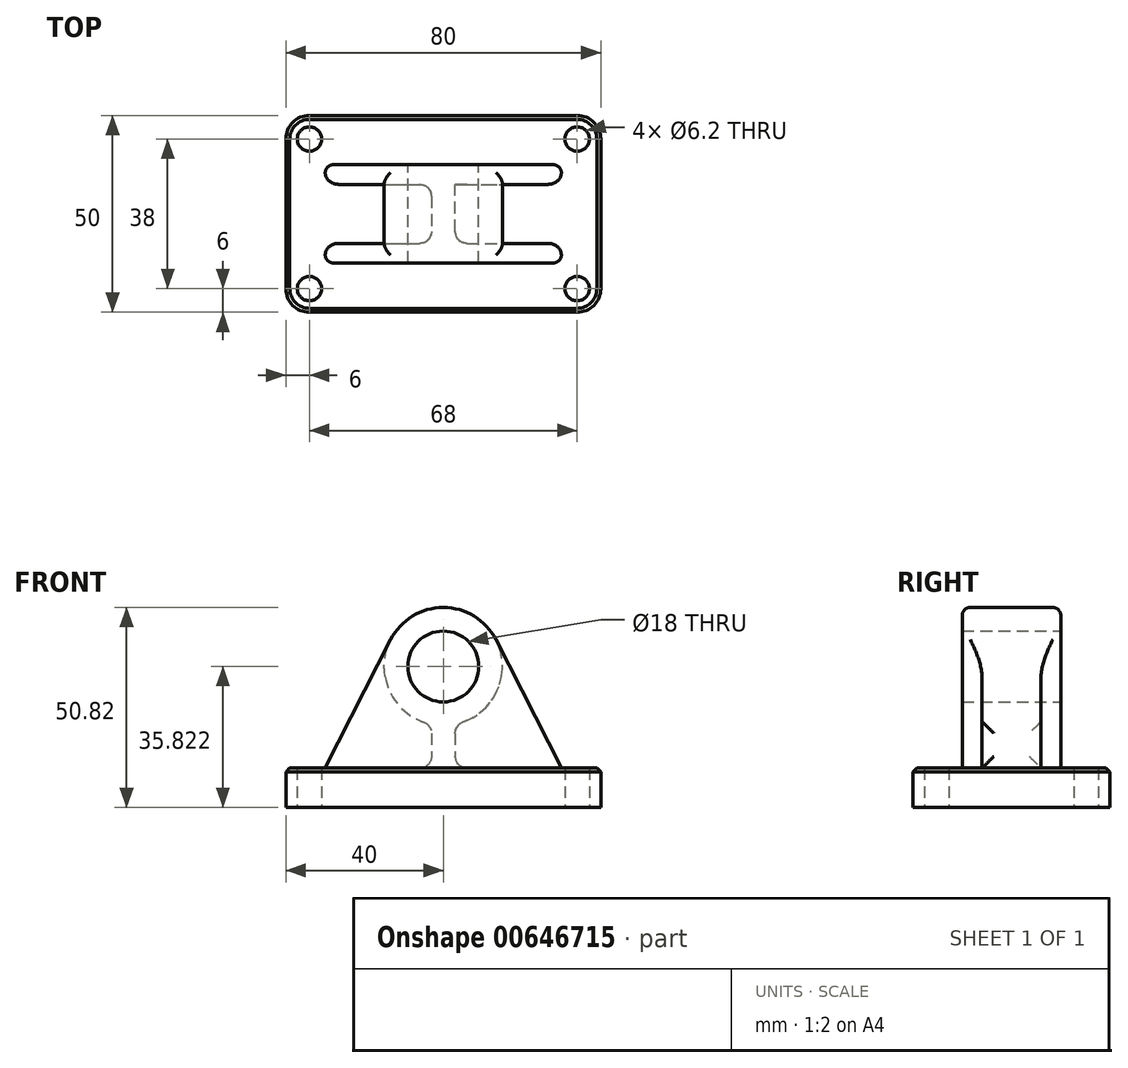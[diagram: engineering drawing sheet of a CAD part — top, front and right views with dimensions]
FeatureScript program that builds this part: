
annotation { "Feature Type Name" : "Feature", "Feature Type Description" : "" }
export const myFeature = defineFeature(function(context is Context, id is Id, definition is map)
    precondition{}
    {
        {
            var Q0;
            Q0=qCreatedBy(makeId("Top.planeOp"),FACE);
            var sketch = newSketch(context, id + "F0", { "sketchPlane" : qUnion([Q0])});
            skLineSegment(sketch, "E0.bottom", {"start": v(34, 25) * mm, "end": v(-34, 25) * mm});
            skLineSegment(sketch, "E0.top", {"start": v(34, -25) * mm, "end": v(-34, -25) * mm});
            skLineSegment(sketch, "E0.left", {"start": v(40, 19) * mm, "end": v(40, -19) * mm});
            skLineSegment(sketch, "E0.right", {"start": v(-40, 19) * mm, "end": v(-40, -19) * mm});
            skPoint(sketch, "E0.middle", {"position": v(0, 0) * mm});
            skPoint(sketch, "E1.visualSharp", {"position": v(-40, 25) * mm});
            skArc(sketch, "E1.filletArc", {"start": v(-34, 25) * mm, "mid": v(-38.24, 23.24) * mm, "end": v(-40, 19) * mm});
            skPoint(sketch, "E2.visualSharp", {"position": v(40, 25) * mm});
            skArc(sketch, "E2.filletArc", {"start": v(40, 19) * mm, "mid": v(38.24, 23.24) * mm, "end": v(34, 25) * mm});
            skPoint(sketch, "E3.visualSharp", {"position": v(40, -25) * mm});
            skArc(sketch, "E3.filletArc", {"start": v(34, -25) * mm, "mid": v(38.24, -23.24) * mm, "end": v(40, -19) * mm});
            skPoint(sketch, "E4.visualSharp", {"position": v(-40, -25) * mm});
            skArc(sketch, "E4.filletArc", {"start": v(-40, -19) * mm, "mid": v(-38.24, -23.24) * mm, "end": v(-34, -25) * mm});
            skCircle(sketch, "E5", {"center": v(-34, 19) * mm, "radius": 3.1 * mm});
            skCircle(sketch, "E6.0.1.0", {"center": v(-34, -19) * mm, "radius": 3.1 * mm});
            skCircle(sketch, "E6.1.0.0", {"center": v(34, 19) * mm, "radius": 3.1 * mm});
            skCircle(sketch, "E6.1.1.0", {"center": v(34, -19) * mm, "radius": 3.1 * mm});
            skLineSegment(sketch, "E6.direction1", {"start": v(-34, 19) * mm, "end": v(34, 19) * mm, "construction": true});
            skLineSegment(sketch, "E6.direction2", {"start": v(-34, 19) * mm, "end": v(-34, -19) * mm, "construction": true});
            skSolve(sketch);
        }
        {
            var Q0;
            Q0=makeQuery(id+"F0.imprint","IMPRINT",FACE,{"disambiguationData":[TD([[makeQuery(id+"F0.imprint","IMPRINT",EDGE,{"derivedFrom":sQuery(id+"F0.wireOp",EDGE,"E0.bottom")}),1.0]])]});
            extrude(context, id + "F1", {"entities" : qUnion([Q0]), "depth" : 10 * mm, "offsetDistance" : 25 * mm});
        }
        {
            var Q0;
            Q0=qCreatedBy(makeId("Front.planeOp"),FACE);
            var sketch = newSketch(context, id + "F2", { "sketchPlane" : qUnion([Q0])});
            skArc(sketch, "E7", {"start": v(3, 21.13) * mm, "mid": v(0, 50.82) * mm, "end": v(-3, 21.13) * mm});
            skCircle(sketch, "E8", {"center": v(0, 35.82) * mm, "radius": 9 * mm});
            skLineSegment(sketch, "E9.top", {"start": v(3, 4.74) * mm, "end": v(-3, 4.74) * mm});
            skLineSegment(sketch, "E9.left", {"start": v(3, 21.13) * mm, "end": v(3, 4.74) * mm});
            skLineSegment(sketch, "E9.right", {"start": v(-3, 21.13) * mm, "end": v(-3, 4.74) * mm});
            skPoint(sketch, "E9.middle", {"position": v(0, 14.08) * mm});
            skPoint(sketch, "E10.orphan", {"position": v(-3, 23.42) * mm});
            skPoint(sketch, "E11.orphan", {"position": v(3, 23.42) * mm});
            skSolve(sketch);
        }
        {
            var Q0;
            Q0 = qSketchRegion(id + "F2", true);
            extrude(context, id + "F3", {"entities" : qUnion([Q0]), "operationType" : NewBodyOperationType.ADD, "endBound" : BoundingType.SYMMETRIC, "depth" : 25 * mm, "offsetDistance" : 25 * mm});
        }
        {
            var Q0;
            Q0=makeQuery(id+"F3.opExtrude","CAP_FACE",FACE,{"disambiguationData":[OSD([sQuery(id+"F2.wireOp",EDGE,"E7"),sQuery(id+"F2.wireOp",EDGE,"E8"),sQuery(id+"F2.wireOp",EDGE,"E9.top"),sQuery(id+"F2.wireOp",EDGE,"E9.left"),sQuery(id+"F2.wireOp",EDGE,"E9.right")])],"isStart":false});
            var sketch = newSketch(context, id + "F4", { "sketchPlane" : qUnion([Q0])});
            skLineSegment(sketch, "E12", {"start": v(-30, 10) * mm, "end": v(-13.36, 42.63) * mm});
            skLineSegment(sketch, "E13", {"start": v(13.36, 42.63) * mm, "end": v(30, 10) * mm});
            skLineSegment(sketch, "E14", {"start": v(0, 0) * mm, "end": v(0, 53.81) * mm, "construction": true});
            skArc(sketch, "E15", {"start": v(-13.36, 42.63) * mm, "mid": v(0, 20.82) * mm, "end": v(13.36, 42.63) * mm});
            skLineSegment(sketch, "E16", {"start": v(-30, 10) * mm, "end": v(30, 10) * mm});
            skSolve(sketch);
        }
        {
            var Q0;
            Q0 = qSketchRegion(id + "F4", true);
            extrude(context, id + "F5", {"entities" : qUnion([Q0]), "operationType" : NewBodyOperationType.ADD, "oppositeDirection" : true, "depth" : 5 * mm, "offsetDistance" : 25 * mm});
        }
        {
            var Q0;
            Q0=makeQuery(id+"F1.opExtrude","SWEPT_BODY",BODY,{"disambiguationData":[OSD([sQuery(id+"F0.wireOp",EDGE,"E0.bottom"),sQuery(id+"F0.wireOp",EDGE,"E0.top"),sQuery(id+"F0.wireOp",EDGE,"E0.left"),sQuery(id+"F0.wireOp",EDGE,"E0.right"),sQuery(id+"F0.wireOp",EDGE,"E1.filletArc"),sQuery(id+"F0.wireOp",EDGE,"E2.filletArc"),sQuery(id+"F0.wireOp",EDGE,"E3.filletArc"),sQuery(id+"F0.wireOp",EDGE,"E4.filletArc"),sQuery(id+"F0.wireOp",EDGE,"E5"),sQuery(id+"F0.wireOp",EDGE,"E6.0.1.0"),sQuery(id+"F0.wireOp",EDGE,"E6.1.0.0"),sQuery(id+"F0.wireOp",EDGE,"E6.1.1.0")])]});
            var Q1;
            Q1=qCreatedBy(makeId("Front.planeOp"),FACE);
            mirror(context, id + "F6", {"operationType" : NewBodyOperationType.ADD, "entities" : qUnion([Q0]), "mirrorPlane" : qUnion([Q1])});
        }
        {
            var Q0;
            Q0=makeQuery(id+"F6.opPattern","COPY",EDGE,{"derivedFrom":makeQuery(id+"F5.opExtrude","CAP_EDGE",EDGE,{"disambiguationData":[OSD([sQuery(id+"F4.wireOp",EDGE,"E12")])],"isStart":true}),"instanceName":"1"});
            var Q1;
            Q1=makeQuery(id+"F3.opExtrude","CAP_EDGE",EDGE,{"disambiguationData":[OSD([sQuery(id+"F2.wireOp",EDGE,"E7")])],"isStart":false});
            fillet(context, id + "F7", {"entities" : qUnion([Q0, Q1]), "radius" : 2 * mm, "tangentPropagation" : true, "allowEdgeOverflow" : false});
        }
        {
            var Q0;
            Q0=makeQuery(id+"F3.opExtrude","SWEPT_FACE",FACE,{"disambiguationData":[OSD([sQuery(id+"F2.wireOp",EDGE,"E9.right")])]});
            var Q1;
            {var subQ1=sQuery(id+"F4.wireOp",EDGE,"E16");Q1=makeQuery(id+"F5.boolean.opBoolean","SPLIT",EDGE,{"disambiguationData":[TD([makeQuery(id+"F3.opExtrude","SWEPT_FACE",FACE,{"disambiguationData":[OSD([sQuery(id+"F2.wireOp",EDGE,"E9.right")])]})])],"derivedFrom":makeQuery(id+"F5.opExtrude","CAP_EDGE",EDGE,{"disambiguationData":[OSD([subQ1])],"isStart":false})});}
            var Q2;
            Q2=makeQuery(id+"F6.opPattern","COPY",EDGE,{"derivedFrom":makeQuery(id+"F5.opExtrude","SWEPT_EDGE",EDGE,{"disambiguationData":[OSD([sQuery(id+"F4.wireOp",EDGE,"E12"),sQuery(id+"F4.wireOp",EDGE,"E16")])]}),"instanceName":"1"});
            var Q3;
            Q3=makeQuery(id+"F5.opExtrude","SWEPT_EDGE",EDGE,{"disambiguationData":[OSD([sQuery(id+"F4.wireOp",EDGE,"E12"),sQuery(id+"F4.wireOp",EDGE,"E16")])]});
            var Q4;
            {var subQ1=sQuery(id+"F4.wireOp",EDGE,"E16");Q4=makeQuery(id+"F6.opPattern","COPY",EDGE,{"derivedFrom":makeQuery(id+"F5.boolean.opBoolean","SPLIT",EDGE,{"disambiguationData":[TD([makeQuery(id+"F3.opExtrude","SWEPT_FACE",FACE,{"disambiguationData":[OSD([sQuery(id+"F2.wireOp",EDGE,"E9.right")])]})])],"derivedFrom":makeQuery(id+"F5.opExtrude","CAP_EDGE",EDGE,{"disambiguationData":[OSD([subQ1])],"isStart":false})}),"instanceName":"1"});}
            var Q5;
            {var subQ0=sQuery(id+"F2.wireOp",EDGE,"E9.right");var subQ1=sQuery(id+"F2.wireOp",EDGE,"E9.left");var subQ2=sQuery(id+"F2.wireOp",EDGE,"E9.top");var subQ3=sQuery(id+"F2.wireOp",EDGE,"E8");var subQ4=sQuery(id+"F2.wireOp",EDGE,"E7");var subQ5=makeQuery(id+"F1.opExtrude","CAP_FACE",FACE,{"disambiguationData":[OSD([sQuery(id+"F0.wireOp",EDGE,"E0.bottom"),sQuery(id+"F0.wireOp",EDGE,"E0.top"),sQuery(id+"F0.wireOp",EDGE,"E0.left"),sQuery(id+"F0.wireOp",EDGE,"E0.right"),sQuery(id+"F0.wireOp",EDGE,"E1.filletArc"),sQuery(id+"F0.wireOp",EDGE,"E2.filletArc"),sQuery(id+"F0.wireOp",EDGE,"E3.filletArc"),sQuery(id+"F0.wireOp",EDGE,"E4.filletArc"),sQuery(id+"F0.wireOp",EDGE,"E5"),sQuery(id+"F0.wireOp",EDGE,"E6.0.1.0"),sQuery(id+"F0.wireOp",EDGE,"E6.1.0.0"),sQuery(id+"F0.wireOp",EDGE,"E6.1.1.0")])],"isStart":false});Q5=makeQuery(id+"F6.boolean.opBoolean","MERGE",EDGE,{"derivedFrom":[makeQuery(id+"F3.boolean.opBoolean","INTERSECT",EDGE,{"derivedFrom":[subQ5,makeQuery(id+"F3.opExtrude","CAP_FACE",FACE,{"disambiguationData":[OSD([subQ4,subQ3,subQ2,subQ1,subQ0])],"isStart":true})]}),makeQuery(id+"F6.opPattern","COPY",EDGE,{"derivedFrom":makeQuery(id+"F5.boolean.opBoolean","MERGE",EDGE,{"derivedFrom":[makeQuery(id+"F3.boolean.opBoolean","INTERSECT",EDGE,{"derivedFrom":[subQ5,makeQuery(id+"F3.opExtrude","CAP_FACE",FACE,{"disambiguationData":[OSD([subQ4,subQ3,subQ2,subQ1,subQ0])],"isStart":false})]}),makeQuery(id+"F5.opExtrude","CAP_EDGE",EDGE,{"disambiguationData":[OSD([sQuery(id+"F4.wireOp",EDGE,"E16")])],"isStart":true})]}),"instanceName":"1"})]});}
            var Q6;
            Q6=makeQuery(id+"F6.opPattern","COPY",EDGE,{"derivedFrom":makeQuery(id+"F5.opExtrude","SWEPT_EDGE",EDGE,{"disambiguationData":[OSD([sQuery(id+"F4.wireOp",EDGE,"E13"),sQuery(id+"F4.wireOp",EDGE,"E16")])]}),"instanceName":"1"});
            var Q7;
            {var subQ0=sQuery(id+"F4.wireOp",EDGE,"E16");Q7=makeQuery(id+"F6.opPattern","COPY",EDGE,{"derivedFrom":makeQuery(id+"F5.boolean.opBoolean","SPLIT",EDGE,{"disambiguationData":[TD([makeQuery(id+"F3.opExtrude","SWEPT_FACE",FACE,{"disambiguationData":[OSD([sQuery(id+"F2.wireOp",EDGE,"E9.left")])]})])],"derivedFrom":makeQuery(id+"F5.opExtrude","CAP_EDGE",EDGE,{"disambiguationData":[OSD([subQ0])],"isStart":false})}),"instanceName":"1"});}
            var Q8;
            {var subQ0=sQuery(id+"F4.wireOp",EDGE,"E15");Q8=makeQuery(id+"F6.opPattern","COPY",EDGE,{"derivedFrom":makeQuery(id+"F5.boolean.opBoolean","SPLIT",EDGE,{"disambiguationData":[TD([makeQuery(id+"F3.opExtrude","SWEPT_FACE",FACE,{"disambiguationData":[OSD([sQuery(id+"F2.wireOp",EDGE,"E9.left")])]})])],"derivedFrom":makeQuery(id+"F5.opExtrude","CAP_EDGE",EDGE,{"disambiguationData":[OSD([subQ0])],"isStart":false})}),"instanceName":"1"});}
            var Q9;
            Q9=makeQuery(id+"F3.boolean.opBoolean","INTERSECT",EDGE,{"derivedFrom":[makeQuery(id+"F1.opExtrude","CAP_FACE",FACE,{"disambiguationData":[OSD([sQuery(id+"F0.wireOp",EDGE,"E0.bottom"),sQuery(id+"F0.wireOp",EDGE,"E0.top"),sQuery(id+"F0.wireOp",EDGE,"E0.left"),sQuery(id+"F0.wireOp",EDGE,"E0.right"),sQuery(id+"F0.wireOp",EDGE,"E1.filletArc"),sQuery(id+"F0.wireOp",EDGE,"E2.filletArc"),sQuery(id+"F0.wireOp",EDGE,"E3.filletArc"),sQuery(id+"F0.wireOp",EDGE,"E4.filletArc"),sQuery(id+"F0.wireOp",EDGE,"E5"),sQuery(id+"F0.wireOp",EDGE,"E6.0.1.0"),sQuery(id+"F0.wireOp",EDGE,"E6.1.0.0"),sQuery(id+"F0.wireOp",EDGE,"E6.1.1.0")])],"isStart":false}),makeQuery(id+"F3.opExtrude","SWEPT_FACE",FACE,{"disambiguationData":[OSD([sQuery(id+"F2.wireOp",EDGE,"E9.left")])]})]});
            var Q10;
            Q10=makeQuery(id+"F5.boolean.opBoolean","INTERSECT",EDGE,{"derivedFrom":[makeQuery(id+"F3.opExtrude","SWEPT_FACE",FACE,{"disambiguationData":[OSD([sQuery(id+"F2.wireOp",EDGE,"E9.left")])]}),makeQuery(id+"F5.opExtrude","CAP_FACE",FACE,{"disambiguationData":[OSD([sQuery(id+"F4.wireOp",EDGE,"E12"),sQuery(id+"F4.wireOp",EDGE,"E13"),sQuery(id+"F4.wireOp",EDGE,"E15"),sQuery(id+"F4.wireOp",EDGE,"E16")])],"isStart":false})]});
            var Q11;
            {var subQ0=sQuery(id+"F4.wireOp",EDGE,"E16");Q11=makeQuery(id+"F5.boolean.opBoolean","SPLIT",EDGE,{"disambiguationData":[TD([makeQuery(id+"F3.opExtrude","SWEPT_FACE",FACE,{"disambiguationData":[OSD([sQuery(id+"F2.wireOp",EDGE,"E9.left")])]})])],"derivedFrom":makeQuery(id+"F5.opExtrude","CAP_EDGE",EDGE,{"disambiguationData":[OSD([subQ0])],"isStart":false})});}
            var Q12;
            Q12=makeQuery(id+"F3.opExtrude","SWEPT_EDGE",EDGE,{"disambiguationData":[OSD([sQuery(id+"F2.wireOp",EDGE,"E7"),sQuery(id+"F2.wireOp",EDGE,"E9.left")])]});
            var Q13;
            {var subQ0=sQuery(id+"F4.wireOp",EDGE,"E15");Q13=makeQuery(id+"F5.boolean.opBoolean","SPLIT",EDGE,{"disambiguationData":[TD([makeQuery(id+"F3.opExtrude","SWEPT_FACE",FACE,{"disambiguationData":[OSD([sQuery(id+"F2.wireOp",EDGE,"E9.left")])]})])],"derivedFrom":makeQuery(id+"F5.opExtrude","CAP_EDGE",EDGE,{"disambiguationData":[OSD([subQ0])],"isStart":false})});}
            var Q14;
            Q14=makeQuery(id+"F5.opExtrude","SWEPT_EDGE",EDGE,{"disambiguationData":[OSD([sQuery(id+"F4.wireOp",EDGE,"E13"),sQuery(id+"F4.wireOp",EDGE,"E16")])]});
            var Q15;
            Q15=makeQuery(id+"F5.boolean.opBoolean","MERGE",EDGE,{"derivedFrom":[makeQuery(id+"F3.boolean.opBoolean","INTERSECT",EDGE,{"derivedFrom":[makeQuery(id+"F1.opExtrude","CAP_FACE",FACE,{"disambiguationData":[OSD([sQuery(id+"F0.wireOp",EDGE,"E0.bottom"),sQuery(id+"F0.wireOp",EDGE,"E0.top"),sQuery(id+"F0.wireOp",EDGE,"E0.left"),sQuery(id+"F0.wireOp",EDGE,"E0.right"),sQuery(id+"F0.wireOp",EDGE,"E1.filletArc"),sQuery(id+"F0.wireOp",EDGE,"E2.filletArc"),sQuery(id+"F0.wireOp",EDGE,"E3.filletArc"),sQuery(id+"F0.wireOp",EDGE,"E4.filletArc"),sQuery(id+"F0.wireOp",EDGE,"E5"),sQuery(id+"F0.wireOp",EDGE,"E6.0.1.0"),sQuery(id+"F0.wireOp",EDGE,"E6.1.0.0"),sQuery(id+"F0.wireOp",EDGE,"E6.1.1.0")])],"isStart":false}),makeQuery(id+"F3.opExtrude","CAP_FACE",FACE,{"disambiguationData":[OSD([sQuery(id+"F2.wireOp",EDGE,"E7"),sQuery(id+"F2.wireOp",EDGE,"E8"),sQuery(id+"F2.wireOp",EDGE,"E9.top"),sQuery(id+"F2.wireOp",EDGE,"E9.left"),sQuery(id+"F2.wireOp",EDGE,"E9.right")])],"isStart":false})]}),makeQuery(id+"F5.opExtrude","CAP_EDGE",EDGE,{"disambiguationData":[OSD([sQuery(id+"F4.wireOp",EDGE,"E16")])],"isStart":true})]});
            var Q16;
            Q16=makeQuery(id+"F5.opExtrude","CAP_EDGE",EDGE,{"disambiguationData":[OSD([sQuery(id+"F4.wireOp",EDGE,"E13")])],"isStart":false});
            var Q17;
            Q17=makeQuery(id+"F6.opPattern","COPY",EDGE,{"derivedFrom":makeQuery(id+"F5.opExtrude","CAP_EDGE",EDGE,{"disambiguationData":[OSD([sQuery(id+"F4.wireOp",EDGE,"E13")])],"isStart":false}),"instanceName":"1"});
            var Q18;
            Q18=makeQuery(id+"F6.opPattern","COPY",EDGE,{"derivedFrom":makeQuery(id+"F5.opExtrude","CAP_EDGE",EDGE,{"disambiguationData":[OSD([sQuery(id+"F4.wireOp",EDGE,"E12")])],"isStart":false}),"instanceName":"1"});
            var Q19;
            Q19=makeQuery(id+"F5.opExtrude","CAP_EDGE",EDGE,{"disambiguationData":[OSD([sQuery(id+"F4.wireOp",EDGE,"E12")])],"isStart":false});
            var Q20;
            {var subQ0=sQuery(id+"F4.wireOp",EDGE,"E15");Q20=makeQuery(id+"F6.opPattern","COPY",EDGE,{"derivedFrom":makeQuery(id+"F5.boolean.opBoolean","SPLIT",EDGE,{"disambiguationData":[TD([makeQuery(id+"F3.opExtrude","SWEPT_FACE",FACE,{"disambiguationData":[OSD([sQuery(id+"F2.wireOp",EDGE,"E9.right")])]})])],"derivedFrom":makeQuery(id+"F5.opExtrude","CAP_EDGE",EDGE,{"disambiguationData":[OSD([subQ0])],"isStart":false})}),"instanceName":"1"});}
            var Q21;
            {var subQ0=sQuery(id+"F4.wireOp",EDGE,"E15");Q21=makeQuery(id+"F5.boolean.opBoolean","SPLIT",EDGE,{"disambiguationData":[TD([makeQuery(id+"F3.opExtrude","SWEPT_FACE",FACE,{"disambiguationData":[OSD([sQuery(id+"F2.wireOp",EDGE,"E9.right")])]})])],"derivedFrom":makeQuery(id+"F5.opExtrude","CAP_EDGE",EDGE,{"disambiguationData":[OSD([subQ0])],"isStart":false})});}
            fillet(context, id + "F8", {"entities" : qUnion([Q0, Q1, Q2, Q3, Q4, Q5, Q6, Q7, Q8, Q9, Q10, Q11, Q12, Q13, Q14, Q15, Q16, Q17, Q18, Q19, Q20, Q21]), "radius" : 3 * mm, "tangentPropagation" : true, "allowEdgeOverflow" : false});
        }
        {
            var Q0;
            Q0=makeQuery(id+"F1.opExtrude","CAP_EDGE",EDGE,{"disambiguationData":[OSD([sQuery(id+"F0.wireOp",EDGE,"E0.bottom")])],"isStart":false});
            chamfer(context, id + "F9", {"entities" : qUnion([Q0]), "width" : 1 * mm, "tangentPropagation" : true});
        }
    });
